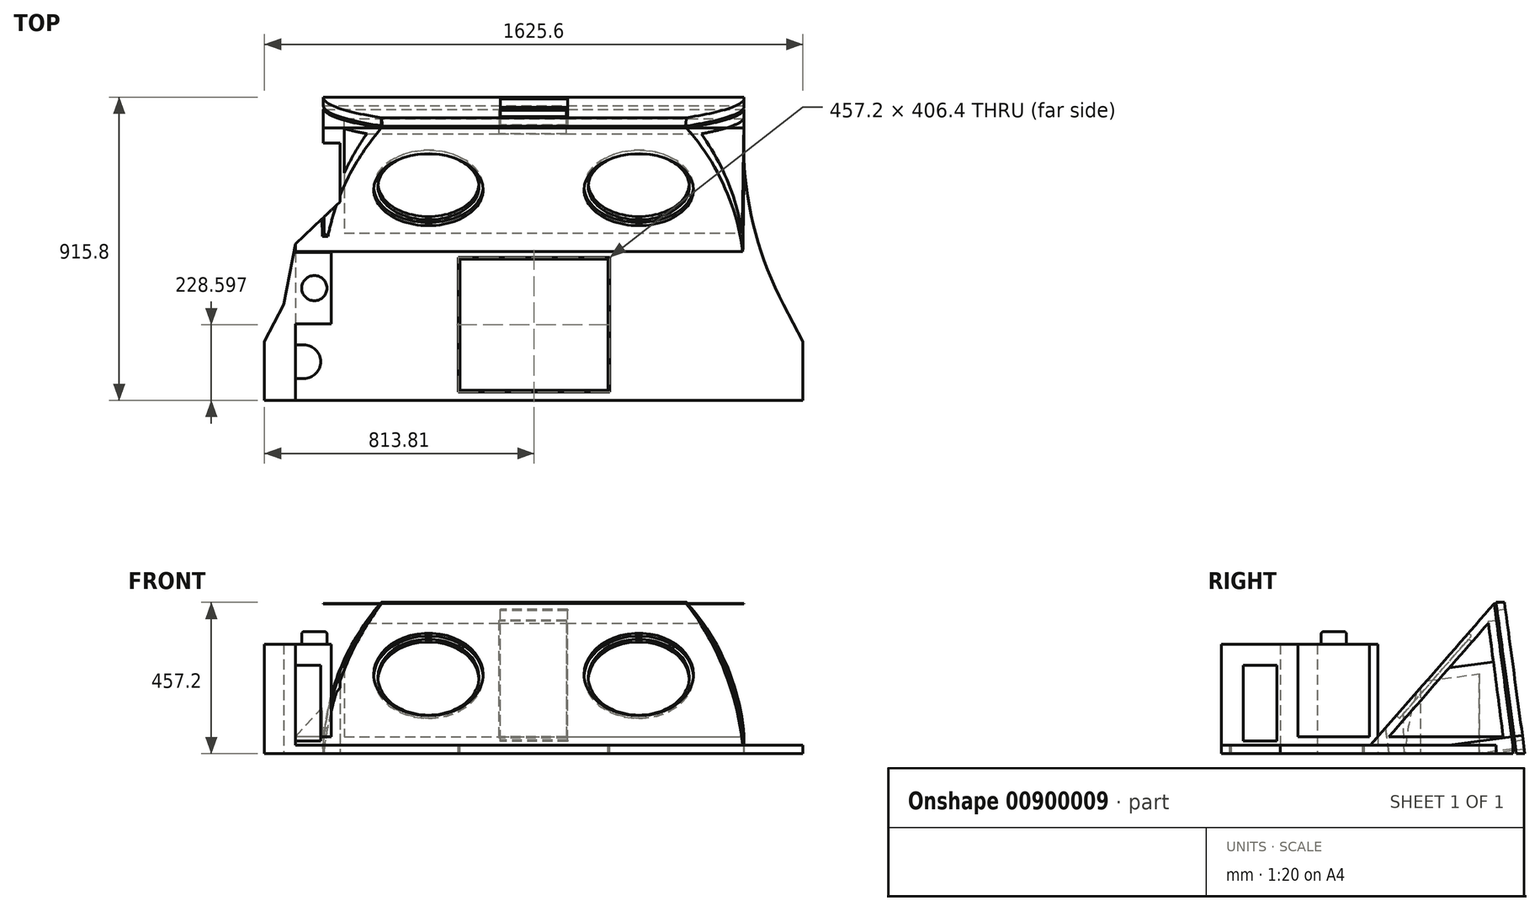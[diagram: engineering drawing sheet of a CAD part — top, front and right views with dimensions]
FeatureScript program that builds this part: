
annotation { "Feature Type Name" : "Feature", "Feature Type Description" : "" }
export const myFeature = defineFeature(function(context is Context, id is Id, definition is map)
    precondition{}
    {
        {
            var Q0;
            Q0=qCreatedBy(makeId("Top.planeOp"),FACE);
            var sketch = newSketch(context, id + "F0", { "sketchPlane" : qUnion([Q0])});
            skLineSegment(sketch, "E0.bottom", {"start": v(-636, 381) * mm, "end": v(634, 381) * mm});
            skLineSegment(sketch, "E1", {"start": v(-636, -498.3) * mm, "end": v(-813.8, -498.3) * mm});
            skLineSegment(sketch, "E2", {"start": v(634, -498.3) * mm, "end": v(811.8, -498.3) * mm});
            skLineSegment(sketch, "E3", {"start": v(-636, -498.3) * mm, "end": v(634, -498.3) * mm});
            skLineSegment(sketch, "E4", {"start": v(-813.8, -498.3) * mm, "end": v(-813.8, -320.5) * mm});
            skLineSegment(sketch, "E5", {"start": v(-636, 381) * mm, "end": v(-636, 279.4) * mm});
            skLineSegment(sketch, "E6", {"start": v(-636, 279.4) * mm, "end": v(-585.2, 279.4) * mm});
            skLineSegment(sketch, "E7", {"start": v(-585.2, 279.4) * mm, "end": v(-585.2, 101.6) * mm});
            skLineSegment(sketch, "E8", {"start": v(-585.2, 101.6) * mm, "end": v(-720.27, -26) * mm});
            skLineSegment(sketch, "E9", {"start": v(634, 381) * mm, "end": v(634, 279.4) * mm});
            skLineSegment(sketch, "E10", {"start": v(634, 279.4) * mm, "end": v(583.2, 279.4) * mm});
            skLineSegment(sketch, "E11", {"start": v(583.2, 279.4) * mm, "end": v(583.2, 101.6) * mm});
            skLineSegment(sketch, "E12", {"start": v(583.2, 101.6) * mm, "end": v(718.25, -26) * mm});
            skLineSegment(sketch, "E13", {"start": v(811.8, -320.5) * mm, "end": v(811.8, -498.3) * mm});
            skLineSegment(sketch, "E14", {"start": v(-813.8, -320.5) * mm, "end": v(-755.4, -208.82) * mm});
            skLineSegment(sketch, "E15", {"start": v(-755.4, -208.82) * mm, "end": v(-720.27, -26) * mm});
            skLineSegment(sketch, "E16", {"start": v(811.8, -320.5) * mm, "end": v(753.38, -208.82) * mm});
            skLineSegment(sketch, "E17", {"start": v(753.38, -208.82) * mm, "end": v(718.25, -26) * mm});
            skSolve(sketch);
        }
        {
            var Q0;
            Q0=qSketchRegion(id+"F0",true);
            extrude(context, id + "F1", {"entities" : qUnion([Q0]), "depth" : 25.4 * mm, "offsetDistance" : 25.4 * mm});
        }
        {
            var Q0;
            Q0=makeQuery(id+"F1.opExtrude","SWEPT_FACE",FACE,{"disambiguationData":[OSD([sQuery(id+"F0.wireOp",EDGE,"E9")])]});
            var sketch = newSketch(context, id + "F2", { "sketchPlane" : qUnion([Q0])});
            skPoint(sketch, "E18.endSnap0", {"position": v(330.2, 0) * mm});
            skLineSegment(sketch, "E19", {"start": v(330.2, 457.2) * mm, "end": v(355.6, 457.2) * mm});
            skLineSegment(sketch, "E20", {"start": v(355.6, 457.2) * mm, "end": v(417.5, 0) * mm});
            skLineSegment(sketch, "E21", {"start": v(417.5, 0) * mm, "end": v(392.1, 0) * mm});
            skLineSegment(sketch, "E22", {"start": v(330.2, 457.2) * mm, "end": v(392.1, 0) * mm});
            skSolve(sketch);
        }
        {
            var Q0;
            Q0=qSketchRegion(id+"F2",true);
            extrude(context, id + "F3", {"entities" : qUnion([Q0]), "oppositeDirection" : true, "depth" : 1270 * mm, "offsetDistance" : 25.4 * mm});
        }
        {
            var Q0;
            Q0=makeQuery(id+"F3.opExtrude","SWEPT_FACE",FACE,{"disambiguationData":[OSD([sQuery(id+"F2.wireOp",EDGE,"E22")])]});
            var sketch = newSketch(context, id + "F4", { "sketchPlane" : qUnion([Q0])});
            skLineSegment(sketch, "E23.bottom", {"start": v(101.6, -14.52) * mm, "end": v(-101.6, -14.52) * mm});
            skLineSegment(sketch, "E23.top", {"start": v(101.6, 383.36) * mm, "end": v(-101.6, 383.36) * mm});
            skLineSegment(sketch, "E23.left", {"start": v(101.6, -14.52) * mm, "end": v(101.6, 383.36) * mm});
            skLineSegment(sketch, "E23.right", {"start": v(-101.6, -14.52) * mm, "end": v(-101.6, 383.36) * mm});
            skSolve(sketch);
        }
        {
            var Q0;
            Q0=makeQuery(id+"F1.opExtrude","CAP_FACE",FACE,{"disambiguationData":[OSD([sQuery(id+"F0.wireOp",EDGE,"E0.bottom"),sQuery(id+"F0.wireOp",EDGE,"E1"),sQuery(id+"F0.wireOp",EDGE,"E2"),sQuery(id+"F0.wireOp",EDGE,"E3"),sQuery(id+"F0.wireOp",EDGE,"E4"),sQuery(id+"F0.wireOp",EDGE,"E5"),sQuery(id+"F0.wireOp",EDGE,"E6"),sQuery(id+"F0.wireOp",EDGE,"E7"),sQuery(id+"F0.wireOp",EDGE,"E8"),sQuery(id+"F0.wireOp",EDGE,"E9"),sQuery(id+"F0.wireOp",EDGE,"E10"),sQuery(id+"F0.wireOp",EDGE,"E11"),sQuery(id+"F0.wireOp",EDGE,"E12"),sQuery(id+"F0.wireOp",EDGE,"E13"),sQuery(id+"F0.wireOp",EDGE,"E14"),sQuery(id+"F0.wireOp",EDGE,"E15"),sQuery(id+"F0.wireOp",EDGE,"E16"),sQuery(id+"F0.wireOp",EDGE,"E17")])],"isStart":false});
            var sketch = newSketch(context, id + "F5", { "sketchPlane" : qUnion([Q0])});
            skLineSegment(sketch, "E24.bottom", {"start": v(-228.6, -66.5) * mm, "end": v(228.6, -66.5) * mm});
            skLineSegment(sketch, "E24.top", {"start": v(-228.6, -472.9) * mm, "end": v(228.6, -472.9) * mm});
            skLineSegment(sketch, "E24.left", {"start": v(-228.6, -66.5) * mm, "end": v(-228.6, -472.9) * mm});
            skLineSegment(sketch, "E24.right", {"start": v(228.6, -66.5) * mm, "end": v(228.6, -472.9) * mm});
            skSolve(sketch);
        }
        {
            var Q0;
            Q0=qSketchRegion(id+"F5",true);
            extrude(context, id + "F6", {"entities" : qUnion([Q0]), "operationType" : NewBodyOperationType.REMOVE, "oppositeDirection" : true, "depth" : 25.4 * mm, "offsetDistance" : 25.4 * mm});
        }
        {
            var Q0;
            Q0=makeQuery(id+"F1.opExtrude","CAP_FACE",FACE,{"disambiguationData":[OSD([sQuery(id+"F0.wireOp",EDGE,"E0.bottom"),sQuery(id+"F0.wireOp",EDGE,"E1"),sQuery(id+"F0.wireOp",EDGE,"E2"),sQuery(id+"F0.wireOp",EDGE,"E3"),sQuery(id+"F0.wireOp",EDGE,"E4"),sQuery(id+"F0.wireOp",EDGE,"E5"),sQuery(id+"F0.wireOp",EDGE,"E6"),sQuery(id+"F0.wireOp",EDGE,"E7"),sQuery(id+"F0.wireOp",EDGE,"E8"),sQuery(id+"F0.wireOp",EDGE,"E9"),sQuery(id+"F0.wireOp",EDGE,"E10"),sQuery(id+"F0.wireOp",EDGE,"E11"),sQuery(id+"F0.wireOp",EDGE,"E12"),sQuery(id+"F0.wireOp",EDGE,"E13"),sQuery(id+"F0.wireOp",EDGE,"E14"),sQuery(id+"F0.wireOp",EDGE,"E15"),sQuery(id+"F0.wireOp",EDGE,"E16"),sQuery(id+"F0.wireOp",EDGE,"E17")])],"isStart":false});
            var sketch = newSketch(context, id + "F7", { "sketchPlane" : qUnion([Q0])});
            skLineSegment(sketch, "E25.bottom", {"start": v(223.52, -71.57) * mm, "end": v(-223.52, -71.57) * mm});
            skLineSegment(sketch, "E25.top", {"start": v(223.52, -467.81) * mm, "end": v(-223.52, -467.81) * mm});
            skLineSegment(sketch, "E25.left", {"start": v(223.52, -71.57) * mm, "end": v(223.52, -467.81) * mm});
            skLineSegment(sketch, "E25.right", {"start": v(-223.52, -71.57) * mm, "end": v(-223.52, -467.81) * mm});
            skSolve(sketch);
        }
        {
            var Q0;
            Q0=qSketchRegion(id+"F7",true);
            extrude(context, id + "F8", {"entities" : qUnion([Q0]), "oppositeDirection" : true, "depth" : 25.4 * mm, "offsetDistance" : 25.4 * mm});
        }
        {
            var Q0;
            Q0=makeQuery(id+"F1.opExtrude","SWEPT_FACE",FACE,{"disambiguationData":[OSD([sQuery(id+"F0.wireOp",EDGE,"E9")])]});
            var sketch = newSketch(context, id + "F9", { "sketchPlane" : qUnion([Q0])});
            skLineSegment(sketch, "E26", {"start": v(381, 25.4) * mm, "end": v(324.97, 453.55) * mm});
            skLineSegment(sketch, "E27", {"start": v(324.97, 453.55) * mm, "end": v(-48.98, 25.4) * mm});
            skPoint(sketch, "E28", {"position": v(138, 239.47) * mm});
            skLineSegment(sketch, "E29", {"start": v(-48.98, 25.4) * mm, "end": v(381, 25.4) * mm});
            skLineSegment(sketch, "E30", {"start": v(138, 239.47) * mm, "end": v(381, 25.4) * mm});
            skSolve(sketch);
        }
        {
            var Q0;
            Q0=qSketchRegion(id+"F9",true);
            extrude(context, id + "F10", {"entities" : qUnion([Q0]), "oppositeDirection" : true, "depth" : 1358.9 * mm, "offsetDistance" : 25.4 * mm});
        }
        {
            var Q0;
            Q0=makeQuery(id+"F10.opExtrude","SWEPT_FACE",FACE,{"disambiguationData":[OSD([sQuery(id+"F9.wireOp",EDGE,"E27")])]});
            var sketch = newSketch(context, id + "F11", { "sketchPlane" : qUnion([Q0])});
            skCircle(sketch, "E31", {"center": v(-318.5, 271.15) * mm, "radius": 165.1 * mm});
            skLineSegment(sketch, "E32", {"start": v(634, 555.37) * mm, "end": v(-1, 555.37) * mm});
            skCircle(sketch, "E33", {"center": v(316.5, 271.15) * mm, "radius": 165.1 * mm});
            skLineSegment(sketch, "E34", {"start": v(634, 555.37) * mm, "end": v(634, -13.09) * mm});
            skSolve(sketch);
        }
        {
            var Q0;
            Q0=qSketchRegion(id+"F11",true);
            extrude(context, id + "F12", {"entities" : qUnion([Q0]), "operationType" : NewBodyOperationType.REMOVE, "oppositeDirection" : true, "depth" : 12.7 * mm, "offsetDistance" : 25.4 * mm});
        }
        {
            var Q0;
            Q0=makeQuery(id+"F10.opExtrude","CAP_FACE",FACE,{"disambiguationData":[OSD([sQuery(id+"F9.wireOp",EDGE,"E26"),sQuery(id+"F9.wireOp",EDGE,"E27"),sQuery(id+"F9.wireOp",EDGE,"E29")])],"isStart":true});
            var sketch = newSketch(context, id + "F13", { "sketchPlane" : qUnion([Q0])});
            skLineSegment(sketch, "E35", {"start": v(307.09, 394.46) * mm, "end": v(6.93, 50.8) * mm});
            skLineSegment(sketch, "E36", {"start": v(6.93, 50.8) * mm, "end": v(352.06, 50.8) * mm});
            skLineSegment(sketch, "E37", {"start": v(307.09, 394.46) * mm, "end": v(352.06, 50.8) * mm});
            skSolve(sketch);
        }
        {
            var Q0;
            Q0=qSketchRegion(id+"F13",true);
            extrude(context, id + "F14", {"entities" : qUnion([Q0]), "operationType" : NewBodyOperationType.REMOVE, "oppositeDirection" : true, "depth" : 1206.5 * mm, "offsetDistance" : 25.4 * mm});
        }
        {
            var Q0;
            Q0=makeQuery(id+"F10.opExtrude","SWEPT_FACE",FACE,{"disambiguationData":[OSD([sQuery(id+"F9.wireOp",EDGE,"E26")])]});
            var sketch = newSketch(context, id + "F15", { "sketchPlane" : qUnion([Q0])});
            skLineSegment(sketch, "E38", {"start": v(-97.47, 356.75) * mm, "end": v(105.78, 356.75) * mm});
            skLineSegment(sketch, "E39", {"start": v(-97.47, 356.75) * mm, "end": v(-97.47, 1.38) * mm});
            skLineSegment(sketch, "E40", {"start": v(105.37, 1.15) * mm, "end": v(105.78, 356.75) * mm});
            skLineSegment(sketch, "E41", {"start": v(-97.47, 1.38) * mm, "end": v(105.37, 1.15) * mm});
            skSolve(sketch);
        }
        {
            var Q0;
            Q0=qSketchRegion(id+"F15",true);
            extrude(context, id + "F16", {"entities" : qUnion([Q0]), "operationType" : NewBodyOperationType.REMOVE, "oppositeDirection" : true, "depth" : 25.4 * mm, "offsetDistance" : 25.4 * mm});
        }
        {
            var Q0;
            Q0=makeQuery(id+"F12.boolean.opBoolean","COPY",FACE,{"derivedFrom":makeQuery(id+"F12.opExtrude","CAP_FACE",FACE,{"disambiguationData":[OSD([sQuery(id+"F11.wireOp",EDGE,"E31")])],"isStart":false})});
            var sketch = newSketch(context, id + "F17", { "sketchPlane" : qUnion([Q0])});
            skCircle(sketch, "E42", {"center": v(-318.5, 271.15) * mm, "radius": 152.4 * mm});
            skCircle(sketch, "E43", {"center": v(316.5, 271.15) * mm, "radius": 152.4 * mm});
            skSolve(sketch);
        }
        {
            var Q0;
            Q0=qSketchRegion(id+"F17",true);
            extrude(context, id + "F18", {"entities" : qUnion([Q0]), "operationType" : NewBodyOperationType.REMOVE, "oppositeDirection" : true, "depth" : 25.4 * mm, "offsetDistance" : 25.4 * mm});
        }
        {
            var Q0;
            Q0=qSketchRegion(id+"F4",true);
            extrude(context, id + "F19", {"entities" : qUnion([Q0]), "operationType" : NewBodyOperationType.REMOVE, "oppositeDirection" : true, "depth" : 25.4 * mm, "offsetDistance" : 25.4 * mm});
        }
        {
            var Q0;
            Q0=makeQuery(id+"F3.opExtrude","SWEPT_FACE",FACE,{"disambiguationData":[OSD([sQuery(id+"F2.wireOp",EDGE,"E22")])]});
            var sketch = newSketch(context, id + "F20", { "sketchPlane" : qUnion([Q0])});
            skArc(sketch, "E44", {"start": v(-457.36, 408.76) * mm, "mid": v(-589.79, 194.76) * mm, "end": v(-636, -52.62) * mm});
            skLineSegment(sketch, "E45", {"start": v(-636, 408.76) * mm, "end": v(-457.36, 408.76) * mm});
            skArc(sketch, "E46.MirrorCS", {"start": v(457.36, 408.76) * mm, "mid": v(589.79, 194.76) * mm, "end": v(636, -52.62) * mm});
            skLineSegment(sketch, "E47.MirrorCS", {"start": v(636, 408.76) * mm, "end": v(457.36, 408.76) * mm});
            skSolve(sketch);
        }
        {
            var Q0;
            Q0=qSketchRegion(id+"F20",true);
            var Q1;
            Q1=makeQuery(id+"F20.imprint","IMPRINT",FACE,{"disambiguationData":[TD([[makeQuery(id+"F20.imprint","IMPRINT",EDGE,{"derivedFrom":sQuery(id+"F20.wireOp",EDGE,"E44")}),-1.0]])]});
            var Q2;
            {var subQ0=sQuery(id+"F20.wireOp",EDGE,"E47.MirrorCS");var subQ2=sQuery(id+"F2.wireOp",EDGE,"E22");var subQ4=makeQuery(id+"F3.opExtrude","CAP_EDGE",EDGE,{"disambiguationData":[OSD([subQ2])],"isStart":true});var subQ6=makeQuery(id+"F20.imprint","INTERSECT",VERTEX,{"derivedFrom":[subQ4,subQ0]});Q2=makeQuery(id+"F20.imprint","IMPRINT",FACE,{"disambiguationData":[TD([[makeQuery(id+"F20.imprint","IMPRINT",EDGE,{"disambiguationData":[TD([[subQ6,-1.0]])],"derivedFrom":subQ4}),-1.0]])]});}
            extrude(context, id + "F21", {"entities" : qUnion([Q0, Q1, Q2]), "operationType" : NewBodyOperationType.REMOVE, "oppositeDirection" : true, "depth" : 25.4 * mm, "offsetDistance" : 25.4 * mm});
        }
        {
            var Q0;
            Q0=makeQuery(id+"F3.opExtrude","SWEPT_FACE",FACE,{"disambiguationData":[OSD([sQuery(id+"F2.wireOp",EDGE,"E20")])]});
            var sketch = newSketch(context, id + "F22", { "sketchPlane" : qUnion([Q0])});
            skArc(sketch, "E48", {"start": v(-460.44, 405.35) * mm, "mid": v(-580.18, 216.74) * mm, "end": v(-634, -0.09) * mm});
            skLineSegment(sketch, "E49", {"start": v(-460.44, 405.35) * mm, "end": v(-652.62, 405.35) * mm});
            skLineSegment(sketch, "E50", {"start": v(-652.62, 405.35) * mm, "end": v(-634, -0.09) * mm});
            skSolve(sketch);
        }
        {
            var Q0;
            Q0=qSketchRegion(id+"F22",true);
            extrude(context, id + "F23", {"entities" : qUnion([Q0]), "operationType" : NewBodyOperationType.REMOVE, "oppositeDirection" : true, "depth" : 459.74 * mm, "offsetDistance" : 25.4 * mm});
        }
        {
            var Q0;
            Q0=makeQuery(id+"F1.opExtrude","SWEPT_FACE",FACE,{"disambiguationData":[OSD([sQuery(id+"F0.wireOp",EDGE,"E12")])]});
            var sketch = newSketch(context, id + "F24", { "sketchPlane" : qUnion([Q0])});
            skLineSegment(sketch, "E51.bottom", {"start": v(-539.96, 25.4) * mm, "end": v(-354.16, 25.4) * mm});
            skLineSegment(sketch, "E51.top", {"start": v(-539.96, 0) * mm, "end": v(-354.16, 0) * mm});
            skLineSegment(sketch, "E51.left", {"start": v(-539.96, 25.4) * mm, "end": v(-539.96, 0) * mm});
            skLineSegment(sketch, "E51.right", {"start": v(-354.16, 25.4) * mm, "end": v(-354.16, 0) * mm});
            skSolve(sketch);
        }
        {
            var Q0;
            Q0=qSketchRegion(id+"F24",true);
            extrude(context, id + "F25", {"entities" : qUnion([Q0]), "operationType" : NewBodyOperationType.ADD, "oppositeDirection" : true, "depth" : 127 * mm, "offsetDistance" : 25.4 * mm});
        }
        {
            var Q0;
            Q0=makeQuery(id+"F25.boolean.opBoolean","MERGE",FACE,{"derivedFrom":[makeQuery(id+"F1.opExtrude","CAP_FACE",FACE,{"disambiguationData":[OSD([sQuery(id+"F0.wireOp",EDGE,"E0.bottom"),sQuery(id+"F0.wireOp",EDGE,"E1"),sQuery(id+"F0.wireOp",EDGE,"E2"),sQuery(id+"F0.wireOp",EDGE,"E3"),sQuery(id+"F0.wireOp",EDGE,"E4"),sQuery(id+"F0.wireOp",EDGE,"E5"),sQuery(id+"F0.wireOp",EDGE,"E6"),sQuery(id+"F0.wireOp",EDGE,"E7"),sQuery(id+"F0.wireOp",EDGE,"E8"),sQuery(id+"F0.wireOp",EDGE,"E9"),sQuery(id+"F0.wireOp",EDGE,"E10"),sQuery(id+"F0.wireOp",EDGE,"E11"),sQuery(id+"F0.wireOp",EDGE,"E12"),sQuery(id+"F0.wireOp",EDGE,"E13"),sQuery(id+"F0.wireOp",EDGE,"E14"),sQuery(id+"F0.wireOp",EDGE,"E15"),sQuery(id+"F0.wireOp",EDGE,"E16"),sQuery(id+"F0.wireOp",EDGE,"E17")])],"isStart":true}),makeQuery(id+"F25.opExtrude","SWEPT_FACE",FACE,{"disambiguationData":[OSD([sQuery(id+"F24.wireOp",EDGE,"E51.top")])]})]});
            var sketch = newSketch(context, id + "F26", { "sketchPlane" : qUnion([Q0])});
            skArc(sketch, "E52", {"start": v(753.38, 208.82) * mm, "mid": v(657.92, -52.77) * mm, "end": v(634, -330.2) * mm});
            skLineSegment(sketch, "E53", {"start": v(753.38, 208.82) * mm, "end": v(533.17, 208.82) * mm});
            skLineSegment(sketch, "E54", {"start": v(533.17, 208.82) * mm, "end": v(533.17, -330.2) * mm});
            skLineSegment(sketch, "E55", {"start": v(533.17, -330.2) * mm, "end": v(634, -330.2) * mm});
            skSolve(sketch);
        }
        {
            var Q0;
            Q0=qSketchRegion(id+"F26",true);
            extrude(context, id + "F27", {"entities" : qUnion([Q0]), "operationType" : NewBodyOperationType.ADD, "oppositeDirection" : true, "depth" : 25.4 * mm, "offsetDistance" : 25.4 * mm});
        }
        {
            var Q0;
            Q0=makeQuery(id+"F27.boolean.opBoolean","MERGE",FACE,{"derivedFrom":[makeQuery(id+"F25.boolean.opBoolean","MERGE",FACE,{"derivedFrom":[makeQuery(id+"F1.opExtrude","CAP_FACE",FACE,{"disambiguationData":[OSD([sQuery(id+"F0.wireOp",EDGE,"E0.bottom"),sQuery(id+"F0.wireOp",EDGE,"E1"),sQuery(id+"F0.wireOp",EDGE,"E2"),sQuery(id+"F0.wireOp",EDGE,"E3"),sQuery(id+"F0.wireOp",EDGE,"E4"),sQuery(id+"F0.wireOp",EDGE,"E5"),sQuery(id+"F0.wireOp",EDGE,"E6"),sQuery(id+"F0.wireOp",EDGE,"E7"),sQuery(id+"F0.wireOp",EDGE,"E8"),sQuery(id+"F0.wireOp",EDGE,"E9"),sQuery(id+"F0.wireOp",EDGE,"E10"),sQuery(id+"F0.wireOp",EDGE,"E11"),sQuery(id+"F0.wireOp",EDGE,"E12"),sQuery(id+"F0.wireOp",EDGE,"E13"),sQuery(id+"F0.wireOp",EDGE,"E14"),sQuery(id+"F0.wireOp",EDGE,"E15"),sQuery(id+"F0.wireOp",EDGE,"E16"),sQuery(id+"F0.wireOp",EDGE,"E17")])],"isStart":true}),makeQuery(id+"F25.opExtrude","SWEPT_FACE",FACE,{"disambiguationData":[OSD([sQuery(id+"F24.wireOp",EDGE,"E51.top")])]})]}),makeQuery(id+"F27.opExtrude","CAP_FACE",FACE,{"disambiguationData":[OSD([sQuery(id+"F26.wireOp",EDGE,"E52"),sQuery(id+"F26.wireOp",EDGE,"E53"),sQuery(id+"F26.wireOp",EDGE,"E54"),sQuery(id+"F26.wireOp",EDGE,"E55")])],"isStart":true})]});
            var sketch = newSketch(context, id + "F28", { "sketchPlane" : qUnion([Q0])});
            skArc(sketch, "E56", {"start": v(753.38, 208.82) * mm, "mid": v(657.92, -52.77) * mm, "end": v(634, -330.2) * mm});
            skLineSegment(sketch, "E57", {"start": v(753.38, 208.82) * mm, "end": v(763.26, -52.66) * mm});
            skLineSegment(sketch, "E58", {"start": v(763.26, -52.66) * mm, "end": v(634, -330.2) * mm});
            skSolve(sketch);
        }
        {
            var Q0;
            Q0=qSketchRegion(id+"F28",true);
            extrude(context, id + "F29", {"entities" : qUnion([Q0]), "operationType" : NewBodyOperationType.REMOVE, "oppositeDirection" : true, "depth" : 25.4 * mm, "offsetDistance" : 25.4 * mm});
        }
        {
            var Q0;
            Q0=makeQuery(id+"F27.boolean.opBoolean","MERGE",FACE,{"derivedFrom":[makeQuery(id+"F25.boolean.opBoolean","MERGE",FACE,{"derivedFrom":[makeQuery(id+"F1.opExtrude","CAP_FACE",FACE,{"disambiguationData":[OSD([sQuery(id+"F0.wireOp",EDGE,"E0.bottom"),sQuery(id+"F0.wireOp",EDGE,"E1"),sQuery(id+"F0.wireOp",EDGE,"E2"),sQuery(id+"F0.wireOp",EDGE,"E3"),sQuery(id+"F0.wireOp",EDGE,"E4"),sQuery(id+"F0.wireOp",EDGE,"E5"),sQuery(id+"F0.wireOp",EDGE,"E6"),sQuery(id+"F0.wireOp",EDGE,"E7"),sQuery(id+"F0.wireOp",EDGE,"E8"),sQuery(id+"F0.wireOp",EDGE,"E9"),sQuery(id+"F0.wireOp",EDGE,"E10"),sQuery(id+"F0.wireOp",EDGE,"E11"),sQuery(id+"F0.wireOp",EDGE,"E12"),sQuery(id+"F0.wireOp",EDGE,"E13"),sQuery(id+"F0.wireOp",EDGE,"E14"),sQuery(id+"F0.wireOp",EDGE,"E15"),sQuery(id+"F0.wireOp",EDGE,"E16"),sQuery(id+"F0.wireOp",EDGE,"E17")])],"isStart":false}),makeQuery(id+"F25.opExtrude","SWEPT_FACE",FACE,{"disambiguationData":[OSD([sQuery(id+"F24.wireOp",EDGE,"E51.bottom")])]})]}),makeQuery(id+"F27.opExtrude","CAP_FACE",FACE,{"disambiguationData":[OSD([sQuery(id+"F26.wireOp",EDGE,"E52"),sQuery(id+"F26.wireOp",EDGE,"E53"),sQuery(id+"F26.wireOp",EDGE,"E54"),sQuery(id+"F26.wireOp",EDGE,"E55")])],"isStart":false})]});
            var sketch = newSketch(context, id + "F30", { "sketchPlane" : qUnion([Q0])});
            skLineSegment(sketch, "E59", {"start": v(-720.27, -26) * mm, "end": v(-720.27, -498.3) * mm});
            skLineSegment(sketch, "E60", {"start": v(-720.27, -498.3) * mm, "end": v(-745.67, -498.3) * mm});
            skLineSegment(sketch, "E61", {"start": v(-745.67, -158.18) * mm, "end": v(-720.27, -26) * mm});
            skLineSegment(sketch, "E62", {"start": v(-745.67, -498.3) * mm, "end": v(-813.8, -498.3) * mm});
            skLineSegment(sketch, "E63", {"start": v(-813.8, -498.3) * mm, "end": v(-813.8, -320.5) * mm});
            skLineSegment(sketch, "E64", {"start": v(-813.8, -320.5) * mm, "end": v(-755.4, -208.82) * mm});
            skLineSegment(sketch, "E65", {"start": v(-755.4, -208.82) * mm, "end": v(-745.67, -158.18) * mm});
            skSolve(sketch);
        }
        {
            var Q0;
            Q0=qSketchRegion(id+"F30",true);
            extrude(context, id + "F31", {"entities" : qUnion([Q0]), "operationType" : NewBodyOperationType.ADD, "depth" : 304.8 * mm, "offsetDistance" : 25.4 * mm});
        }
        {
            var Q0;
            Q0=makeQuery(id+"F31.opExtrude","SWEPT_FACE",FACE,{"disambiguationData":[OSD([sQuery(id+"F30.wireOp",EDGE,"E59")])]});
            var sketch = newSketch(context, id + "F32", { "sketchPlane" : qUnion([Q0])});
            skLineSegment(sketch, "E66.bottom", {"start": v(-51.4, 330.2) * mm, "end": v(-267.3, 330.2) * mm});
            skLineSegment(sketch, "E66.top", {"start": v(-51.4, 50.8) * mm, "end": v(-267.3, 50.8) * mm});
            skLineSegment(sketch, "E66.left", {"start": v(-51.4, 330.2) * mm, "end": v(-51.4, 50.8) * mm});
            skLineSegment(sketch, "E66.right", {"start": v(-267.3, 330.2) * mm, "end": v(-267.3, 50.8) * mm});
            skSolve(sketch);
        }
        {
            var Q0;
            Q0=qSketchRegion(id+"F32",true);
            extrude(context, id + "F33", {"entities" : qUnion([Q0]), "operationType" : NewBodyOperationType.ADD, "depth" : 107.95 * mm, "offsetDistance" : 25.4 * mm});
        }
        {
            var Q0;
            Q0=makeQuery(id+"F31.opExtrude","SWEPT_FACE",FACE,{"disambiguationData":[OSD([sQuery(id+"F30.wireOp",EDGE,"E59")])]});
            var sketch = newSketch(context, id + "F34", { "sketchPlane" : qUnion([Q0])});
            skLineSegment(sketch, "E67.bottom", {"start": v(-432.4, 266.7) * mm, "end": v(-330.8, 266.7) * mm});
            skLineSegment(sketch, "E67.top", {"start": v(-432.4, 38.1) * mm, "end": v(-330.8, 38.1) * mm});
            skLineSegment(sketch, "E67.left", {"start": v(-432.4, 266.7) * mm, "end": v(-432.4, 38.1) * mm});
            skLineSegment(sketch, "E67.right", {"start": v(-330.8, 266.7) * mm, "end": v(-330.8, 38.1) * mm});
            skSolve(sketch);
        }
        {
            var Q0;
            Q0=qSketchRegion(id+"F34",true);
            extrude(context, id + "F35", {"entities" : qUnion([Q0]), "operationType" : NewBodyOperationType.ADD, "depth" : 76.2 * mm, "offsetDistance" : 25.4 * mm});
        }
        {
            var Q0;
            Q0=makeQuery(id+"F35.opExtrude","CAP_EDGE",EDGE,{"disambiguationData":[OSD([sQuery(id+"F34.wireOp",EDGE,"E67.left")])],"isStart":false});
            fillet(context, id + "F36", {"entities" : qUnion([Q0]), "radius" : 50.8 * mm, "tangentPropagation" : true, "allowEdgeOverflow" : false});
        }
        {
            var Q0;
            Q0=makeQuery(id+"F35.opExtrude","CAP_EDGE",EDGE,{"disambiguationData":[OSD([sQuery(id+"F34.wireOp",EDGE,"E67.right")])],"isStart":false});
            fillet(context, id + "F37", {"entities" : qUnion([Q0]), "radius" : 50.8 * mm, "tangentPropagation" : true, "allowEdgeOverflow" : false});
        }
        {
            var Q0;
            Q0=makeQuery(id+"F33.boolean.opBoolean","MERGE",FACE,{"derivedFrom":[makeQuery(id+"F31.opExtrude","CAP_FACE",FACE,{"disambiguationData":[OSD([sQuery(id+"F30.wireOp",EDGE,"E59"),sQuery(id+"F30.wireOp",EDGE,"E60"),sQuery(id+"F30.wireOp",EDGE,"E61"),sQuery(id+"F30.wireOp",EDGE,"E62"),sQuery(id+"F30.wireOp",EDGE,"E63"),sQuery(id+"F30.wireOp",EDGE,"E64"),sQuery(id+"F30.wireOp",EDGE,"E65")])],"isStart":false}),makeQuery(id+"F33.opExtrude","SWEPT_FACE",FACE,{"disambiguationData":[OSD([sQuery(id+"F32.wireOp",EDGE,"E66.bottom")])]})]});
            var sketch = newSketch(context, id + "F38", { "sketchPlane" : qUnion([Q0])});
            skCircle(sketch, "E68", {"center": v(-663.12, -159.34) * mm, "radius": 38.1 * mm});
            skSolve(sketch);
        }
        {
            var Q0;
            Q0=qSketchRegion(id+"F38",true);
            extrude(context, id + "F39", {"entities" : qUnion([Q0]), "operationType" : NewBodyOperationType.ADD, "depth" : 38.1 * mm, "offsetDistance" : 25.4 * mm});
        }
        {
            var Q0;
            Q0=makeQuery(id+"F39.opExtrude","CAP_FACE",FACE,{"disambiguationData":[OSD([sQuery(id+"F38.wireOp",EDGE,"E68")])],"isStart":false});
            fillet(context, id + "F40", {"entities" : qUnion([Q0]), "radius" : 6.35 * mm, "tangentPropagation" : true, "allowEdgeOverflow" : false});
        }
        {
            var Q0;
            Q0=makeQuery(id+"F27.boolean.opBoolean","MERGE",FACE,{"derivedFrom":[makeQuery(id+"F25.boolean.opBoolean","MERGE",FACE,{"derivedFrom":[makeQuery(id+"F1.opExtrude","CAP_FACE",FACE,{"disambiguationData":[OSD([sQuery(id+"F0.wireOp",EDGE,"E0.bottom"),sQuery(id+"F0.wireOp",EDGE,"E1"),sQuery(id+"F0.wireOp",EDGE,"E2"),sQuery(id+"F0.wireOp",EDGE,"E3"),sQuery(id+"F0.wireOp",EDGE,"E4"),sQuery(id+"F0.wireOp",EDGE,"E5"),sQuery(id+"F0.wireOp",EDGE,"E6"),sQuery(id+"F0.wireOp",EDGE,"E7"),sQuery(id+"F0.wireOp",EDGE,"E8"),sQuery(id+"F0.wireOp",EDGE,"E9"),sQuery(id+"F0.wireOp",EDGE,"E10"),sQuery(id+"F0.wireOp",EDGE,"E11"),sQuery(id+"F0.wireOp",EDGE,"E12"),sQuery(id+"F0.wireOp",EDGE,"E13"),sQuery(id+"F0.wireOp",EDGE,"E14"),sQuery(id+"F0.wireOp",EDGE,"E15"),sQuery(id+"F0.wireOp",EDGE,"E16"),sQuery(id+"F0.wireOp",EDGE,"E17")])],"isStart":true}),makeQuery(id+"F25.opExtrude","SWEPT_FACE",FACE,{"disambiguationData":[OSD([sQuery(id+"F24.wireOp",EDGE,"E51.top")])]})]}),makeQuery(id+"F27.opExtrude","CAP_FACE",FACE,{"disambiguationData":[OSD([sQuery(id+"F26.wireOp",EDGE,"E52"),sQuery(id+"F26.wireOp",EDGE,"E53"),sQuery(id+"F26.wireOp",EDGE,"E54"),sQuery(id+"F26.wireOp",EDGE,"E55")])],"isStart":true})]});
            var sketch = newSketch(context, id + "F41", { "sketchPlane" : qUnion([Q0])});
            skLineSegment(sketch, "E69", {"start": v(-636, -381) * mm, "end": v(-752, -381) * mm});
            skLineSegment(sketch, "E70", {"start": v(-752, -381) * mm, "end": v(-755.4, 78.84) * mm});
            skLineSegment(sketch, "E71", {"start": v(-755.4, 78.84) * mm, "end": v(-724.73, 49.2) * mm});
            skLineSegment(sketch, "E72", {"start": v(-724.73, 49.2) * mm, "end": v(-720.27, 26) * mm});
            skLineSegment(sketch, "E73", {"start": v(-720.27, 26) * mm, "end": v(-585.2, -101.6) * mm});
            skLineSegment(sketch, "E74", {"start": v(-585.2, -101.6) * mm, "end": v(-585.2, -279.4) * mm});
            skLineSegment(sketch, "E75", {"start": v(-585.2, -279.4) * mm, "end": v(-636, -279.4) * mm});
            skLineSegment(sketch, "E76", {"start": v(-636, -279.4) * mm, "end": v(-636, -381) * mm});
            skSolve(sketch);
        }
        {
            var Q0;
            Q0 = qSketchRegion(id + "F41", true);
            extrude(context, id + "F42", {"entities" : qUnion([Q0]), "operationType" : NewBodyOperationType.REMOVE, "oppositeDirection" : true, "depth" : 508 * mm, "offsetDistance" : 25.4 * mm});
        }
        {
            var Q0;
            Q0=makeQuery(id+"F3.opExtrude","SWEPT_FACE",FACE,{"disambiguationData":[OSD([sQuery(id+"F2.wireOp",EDGE,"E20")])]});
            var sketch = newSketch(context, id + "F43", { "sketchPlane" : qUnion([Q0])});
            skArc(sketch, "E77", {"start": v(635.91, -41.07) * mm, "mid": v(586.84, 197.34) * mm, "end": v(460.44, 405.35) * mm});
            skLineSegment(sketch, "E78", {"start": v(460.44, 405.35) * mm, "end": v(645.32, 405.35) * mm});
            skLineSegment(sketch, "E79", {"start": v(645.32, 405.35) * mm, "end": v(635.91, -41.07) * mm});
            skSolve(sketch);
        }
        {
            var Q0;
            Q0 = qSketchRegion(id + "F43", true);
            extrude(context, id + "F44", {"entities" : qUnion([Q0]), "operationType" : NewBodyOperationType.REMOVE, "oppositeDirection" : true, "depth" : 406.4 * mm, "offsetDistance" : 25.4 * mm});
        }
    });
